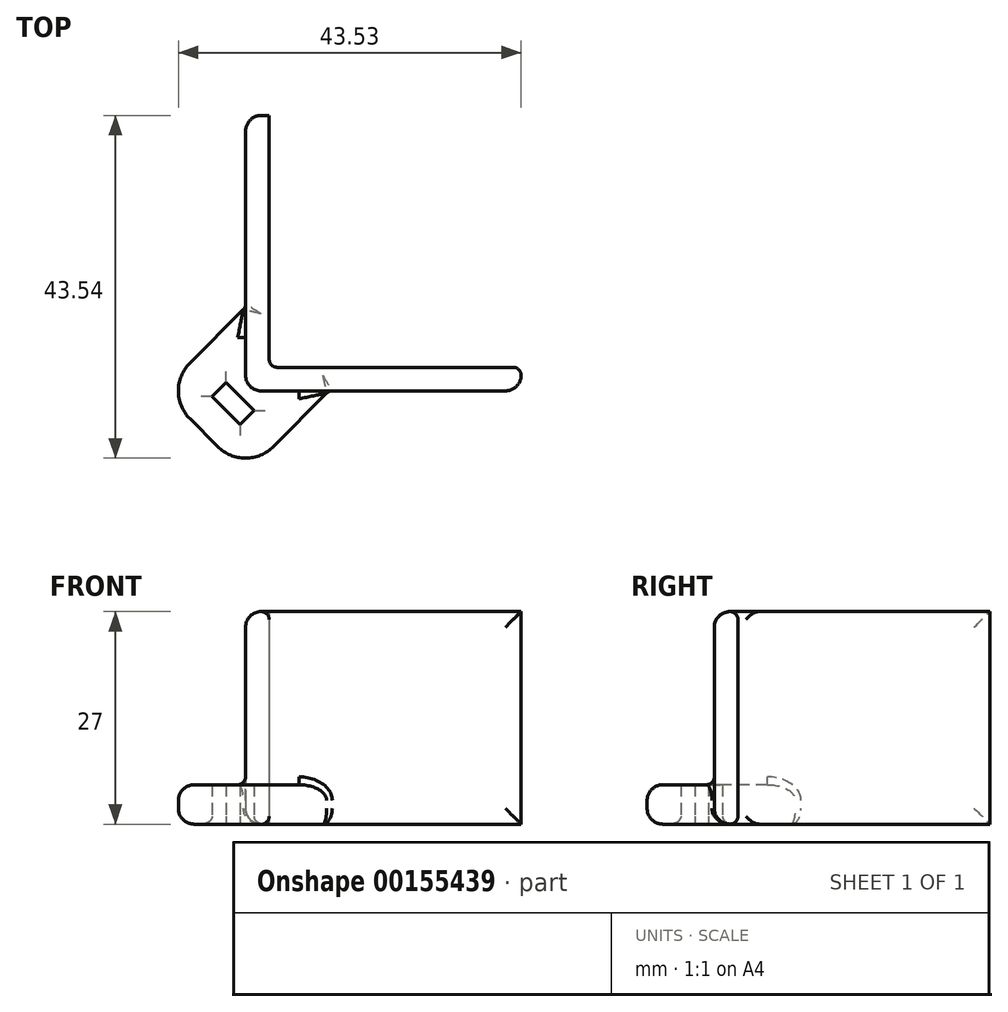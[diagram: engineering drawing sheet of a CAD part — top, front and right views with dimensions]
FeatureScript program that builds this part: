
annotation { "Feature Type Name" : "Feature", "Feature Type Description" : "" }
export const myFeature = defineFeature(function(context is Context, id is Id, definition is map)
    precondition{}
    {
        {
            var Q0;
            Q0=qCreatedBy(makeId("Top.planeOp"),FACE);
            var sketch = newSketch(context, id + "F0", { "sketchPlane" : qUnion([Q0])});
            skLineSegment(sketch, "E0", {"start": v(2.48, 21.6) * mm, "end": v(2.48, -13.4) * mm});
            skLineSegment(sketch, "E1", {"start": v(2.48, -13.4) * mm, "end": v(37.48, -13.4) * mm});
            skLineSegment(sketch, "E2", {"start": v(37.48, -13.4) * mm, "end": v(37.48, -10.4) * mm});
            skLineSegment(sketch, "E3", {"start": v(37.48, -10.4) * mm, "end": v(5.48, -10.4) * mm});
            skLineSegment(sketch, "E4", {"start": v(5.48, -10.4) * mm, "end": v(5.48, 21.6) * mm});
            skLineSegment(sketch, "E5", {"start": v(5.48, 21.6) * mm, "end": v(2.48, 21.6) * mm});
            skLineSegment(sketch, "E6", {"start": v(2.48, -2.8) * mm, "end": v(-8.13, -13.4) * mm});
            skLineSegment(sketch, "E7", {"start": v(-8.13, -13.4) * mm, "end": v(2.48, -24) * mm});
            skLineSegment(sketch, "E8", {"start": v(2.48, -24) * mm, "end": v(13.09, -13.4) * mm});
            skPoint(sketch, "E9.endSnap0", {"position": v(-2.82, -18.7) * mm});
            skLineSegment(sketch, "E10", {"start": v(0, -12.35) * mm, "end": v(3.54, -15.88) * mm});
            skLineSegment(sketch, "E11", {"start": v(3.54, -15.88) * mm, "end": v(1.77, -17.65) * mm});
            skLineSegment(sketch, "E12", {"start": v(1.77, -17.65) * mm, "end": v(-1.77, -14.11) * mm});
            skLineSegment(sketch, "E13", {"start": v(-1.77, -14.11) * mm, "end": v(0, -12.35) * mm});
            skSolve(sketch);
        }
        {
            var Q0;
            Q0=makeQuery(id+"F0.imprint","IMPRINT",FACE,{"disambiguationData":[TD([[makeQuery(id+"F0.imprint","IMPRINT",EDGE,{"derivedFrom":sQuery(id+"F0.wireOp",EDGE,"E0")}),1.0]])]});
            extrude(context, id + "F1", {"entities" : qUnion([Q0]), "depth" : 27 * mm});
        }
        {
            var Q0;
            Q0 = qSketchRegion(id + "F0", true);
            extrude(context, id + "F2", {"entities" : qUnion([Q0]), "operationType" : NewBodyOperationType.ADD, "depth" : 5 * mm});
        }
        {
            var Q0;
            Q0=makeQuery(id+"F1.opExtrude","SWEPT_EDGE",EDGE,{"disambiguationData":[OSD([sQuery(id+"F0.wireOp",EDGE,"E0"),sQuery(id+"F0.wireOp",EDGE,"E1")])]});
            var Q1;
            Q1=makeQuery(id+"F1.opExtrude","CAP_EDGE",EDGE,{"disambiguationData":[OSD([sQuery(id+"F0.wireOp",EDGE,"E1")])],"isStart":false});
            var Q2;
            Q2=makeQuery(id+"F1.opExtrude","CAP_EDGE",EDGE,{"disambiguationData":[OSD([sQuery(id+"F0.wireOp",EDGE,"E0")])],"isStart":false});
            var Q3;
            Q3=makeQuery(id+"F1.opExtrude","CAP_EDGE",EDGE,{"disambiguationData":[OSD([sQuery(id+"F0.wireOp",EDGE,"E1")])],"isStart":true});
            var Q4;
            Q4=makeQuery(id+"F1.opExtrude","SWEPT_EDGE",EDGE,{"disambiguationData":[OSD([sQuery(id+"F0.wireOp",EDGE,"E1"),sQuery(id+"F0.wireOp",EDGE,"E2")])]});
            var Q5;
            Q5=makeQuery(id+"F1.opExtrude","CAP_EDGE",EDGE,{"disambiguationData":[OSD([sQuery(id+"F0.wireOp",EDGE,"E0")])],"isStart":true});
            var Q6;
            Q6=makeQuery(id+"F1.opExtrude","SWEPT_EDGE",EDGE,{"disambiguationData":[OSD([sQuery(id+"F0.wireOp",EDGE,"E0"),sQuery(id+"F0.wireOp",EDGE,"E5")])]});
            var Q7;
            Q7=makeQuery(id+"F2.opExtrude","CAP_EDGE",EDGE,{"disambiguationData":[OSD([sQuery(id+"F0.wireOp",EDGE,"E6")])],"isStart":false});
            var Q8;
            Q8=makeQuery(id+"F2.opExtrude","CAP_EDGE",EDGE,{"disambiguationData":[OSD([sQuery(id+"F0.wireOp",EDGE,"E8")])],"isStart":false});
            var Q9;
            Q9=makeQuery(id+"F2.opExtrude","CAP_EDGE",EDGE,{"disambiguationData":[OSD([sQuery(id+"F0.wireOp",EDGE,"E7")])],"isStart":false});
            var Q10;
            Q10=makeQuery(id+"F2.opExtrude","CAP_EDGE",EDGE,{"disambiguationData":[OSD([sQuery(id+"F0.wireOp",EDGE,"E7")])],"isStart":true});
            var Q11;
            Q11=makeQuery(id+"F2.opExtrude","CAP_EDGE",EDGE,{"disambiguationData":[OSD([sQuery(id+"F0.wireOp",EDGE,"E6")])],"isStart":true});
            var Q12;
            Q12=makeQuery(id+"F2.opExtrude","CAP_EDGE",EDGE,{"disambiguationData":[OSD([sQuery(id+"F0.wireOp",EDGE,"E8")])],"isStart":true});
            fillet(context, id + "F3", {"entities" : qUnion([Q0, Q1, Q2, Q3, Q4, Q5, Q6, Q7, Q8, Q9, Q10, Q11, Q12]), "radius" : 2 * mm, "tangentPropagation" : true, "allowEdgeOverflow" : false});
        }
        {
            var Q0;
            Q0=makeQuery(id+"F2.opExtrude","SWEPT_EDGE",EDGE,{"disambiguationData":[OSD([sQuery(id+"F0.wireOp",EDGE,"E6"),sQuery(id+"F0.wireOp",EDGE,"E7")])]});
            var Q1;
            Q1=makeQuery(id+"F2.opExtrude","SWEPT_EDGE",EDGE,{"disambiguationData":[OSD([sQuery(id+"F0.wireOp",EDGE,"E7"),sQuery(id+"F0.wireOp",EDGE,"E8")])]});
            var Q2;
            Q2=makeQuery(id+"F2.opExtrude","SWEPT_EDGE",EDGE,{"disambiguationData":[OSD([sQuery(id+"F0.wireOp",EDGE,"E0"),sQuery(id+"F0.wireOp",EDGE,"E6")])]});
            fillet(context, id + "F4", {"entities" : qUnion([Q0, Q1, Q2]), "radius" : 5 * mm, "tangentPropagation" : true, "allowEdgeOverflow" : false});
        }
        {
            var Q0;
            {var subQ0=sQuery(id+"F0.wireOp",EDGE,"E5");var subQ1=sQuery(id+"F0.wireOp",EDGE,"E4");var subQ2=sQuery(id+"F0.wireOp",EDGE,"E3");var subQ3=sQuery(id+"F0.wireOp",EDGE,"E2");var subQ4=sQuery(id+"F0.wireOp",EDGE,"E1");var subQ5=sQuery(id+"F0.wireOp",EDGE,"E0");Q0=makeQuery(id+"F3.opFillet","BLEND_EDGE",EDGE,{"blendedFrom":[makeQuery(id+"F1.opExtrude","CAP_EDGE",EDGE,{"disambiguationData":[OSD([subQ5])],"isStart":true}),makeQuery(id+"F2.boolean.opBoolean","MERGE",FACE,{"derivedFrom":[makeQuery(id+"F1.opExtrude","CAP_FACE",FACE,{"disambiguationData":[OSD([subQ5,subQ4,subQ3,subQ2,subQ1,subQ0])],"isStart":true}),makeQuery(id+"F2.opExtrude","CAP_FACE",FACE,{"disambiguationData":[OSD([subQ5,subQ4,subQ3,subQ2,subQ1,subQ0,sQuery(id+"F0.wireOp",EDGE,"E6"),sQuery(id+"F0.wireOp",EDGE,"E7"),sQuery(id+"F0.wireOp",EDGE,"E8"),sQuery(id+"F0.wireOp",EDGE,"E10"),sQuery(id+"F0.wireOp",EDGE,"E11"),sQuery(id+"F0.wireOp",EDGE,"E12"),sQuery(id+"F0.wireOp",EDGE,"E13")])],"isStart":true})]})],"blendedInto":[makeQuery(id+"F2.boolean.opBoolean","MERGE",FACE,{"derivedFrom":[makeQuery(id+"F1.opExtrude","CAP_FACE",FACE,{"disambiguationData":[OSD([subQ5,subQ4,subQ3,subQ2,subQ1,subQ0])],"isStart":true}),makeQuery(id+"F2.opExtrude","CAP_FACE",FACE,{"disambiguationData":[OSD([subQ5,subQ4,subQ3,subQ2,subQ1,subQ0,sQuery(id+"F0.wireOp",EDGE,"E6"),sQuery(id+"F0.wireOp",EDGE,"E7"),sQuery(id+"F0.wireOp",EDGE,"E8"),sQuery(id+"F0.wireOp",EDGE,"E10"),sQuery(id+"F0.wireOp",EDGE,"E11"),sQuery(id+"F0.wireOp",EDGE,"E12"),sQuery(id+"F0.wireOp",EDGE,"E13")])],"isStart":true})]})]});}
            var Q1;
            Q1=makeQuery(id+"F1.opExtrude","SWEPT_FACE",FACE,{"disambiguationData":[OSD([sQuery(id+"F0.wireOp",EDGE,"E1")])]});
            var Q2;
            Q2=makeQuery(id+"F1.opExtrude","SWEPT_FACE",FACE,{"disambiguationData":[OSD([sQuery(id+"F0.wireOp",EDGE,"E3")])]});
            var Q3;
            {var subQ0=sQuery(id+"F0.wireOp",EDGE,"E10");var subQ1=sQuery(id+"F0.wireOp",EDGE,"E1");var subQ2=sQuery(id+"F0.wireOp",EDGE,"E0");Q3=makeQuery(id+"F4.opFillet","BLEND_EDGE",EDGE,{"blendedFrom":[makeQuery(id+"F3.opFillet","BLEND_EDGE",EDGE,{"blendedFrom":[makeQuery(id+"F1.opExtrude","SWEPT_EDGE",EDGE,{"disambiguationData":[OSD([subQ2,subQ1])]}),makeQuery(id+"F2.opExtrude","CAP_FACE",FACE,{"disambiguationData":[OSD([subQ2,subQ1,sQuery(id+"F0.wireOp",EDGE,"E2"),sQuery(id+"F0.wireOp",EDGE,"E3"),sQuery(id+"F0.wireOp",EDGE,"E4"),sQuery(id+"F0.wireOp",EDGE,"E5"),sQuery(id+"F0.wireOp",EDGE,"E6"),sQuery(id+"F0.wireOp",EDGE,"E7"),sQuery(id+"F0.wireOp",EDGE,"E8"),subQ0,sQuery(id+"F0.wireOp",EDGE,"E11"),sQuery(id+"F0.wireOp",EDGE,"E12"),sQuery(id+"F0.wireOp",EDGE,"E13")])],"isStart":false})],"blendedInto":[makeQuery(id+"F2.opExtrude","CAP_FACE",FACE,{"disambiguationData":[OSD([subQ2,subQ1,sQuery(id+"F0.wireOp",EDGE,"E2"),sQuery(id+"F0.wireOp",EDGE,"E3"),sQuery(id+"F0.wireOp",EDGE,"E4"),sQuery(id+"F0.wireOp",EDGE,"E5"),sQuery(id+"F0.wireOp",EDGE,"E6"),sQuery(id+"F0.wireOp",EDGE,"E7"),sQuery(id+"F0.wireOp",EDGE,"E8"),subQ0,sQuery(id+"F0.wireOp",EDGE,"E11"),sQuery(id+"F0.wireOp",EDGE,"E12"),sQuery(id+"F0.wireOp",EDGE,"E13")])],"isStart":false})]}),makeQuery(id+"F2.opExtrude","SWEPT_FACE",FACE,{"disambiguationData":[OSD([subQ0])]})],"blendedInto":[makeQuery(id+"F2.opExtrude","SWEPT_FACE",FACE,{"disambiguationData":[OSD([subQ0])]})]});}
            var Q4;
            {var subQ0=sQuery(id+"F0.wireOp",EDGE,"E13");var subQ1=sQuery(id+"F0.wireOp",EDGE,"E1");var subQ2=sQuery(id+"F0.wireOp",EDGE,"E0");Q4=makeQuery(id+"F4.opFillet","BLEND_EDGE",EDGE,{"blendedFrom":[makeQuery(id+"F3.opFillet","BLEND_EDGE",EDGE,{"blendedFrom":[makeQuery(id+"F1.opExtrude","SWEPT_EDGE",EDGE,{"disambiguationData":[OSD([subQ2,subQ1])]}),makeQuery(id+"F2.opExtrude","CAP_FACE",FACE,{"disambiguationData":[OSD([subQ2,subQ1,sQuery(id+"F0.wireOp",EDGE,"E2"),sQuery(id+"F0.wireOp",EDGE,"E3"),sQuery(id+"F0.wireOp",EDGE,"E4"),sQuery(id+"F0.wireOp",EDGE,"E5"),sQuery(id+"F0.wireOp",EDGE,"E6"),sQuery(id+"F0.wireOp",EDGE,"E7"),sQuery(id+"F0.wireOp",EDGE,"E8"),sQuery(id+"F0.wireOp",EDGE,"E10"),sQuery(id+"F0.wireOp",EDGE,"E11"),sQuery(id+"F0.wireOp",EDGE,"E12"),subQ0])],"isStart":false})],"blendedInto":[makeQuery(id+"F2.opExtrude","CAP_FACE",FACE,{"disambiguationData":[OSD([subQ2,subQ1,sQuery(id+"F0.wireOp",EDGE,"E2"),sQuery(id+"F0.wireOp",EDGE,"E3"),sQuery(id+"F0.wireOp",EDGE,"E4"),sQuery(id+"F0.wireOp",EDGE,"E5"),sQuery(id+"F0.wireOp",EDGE,"E6"),sQuery(id+"F0.wireOp",EDGE,"E7"),sQuery(id+"F0.wireOp",EDGE,"E8"),sQuery(id+"F0.wireOp",EDGE,"E10"),sQuery(id+"F0.wireOp",EDGE,"E11"),sQuery(id+"F0.wireOp",EDGE,"E12"),subQ0])],"isStart":false})]}),makeQuery(id+"F2.opExtrude","SWEPT_FACE",FACE,{"disambiguationData":[OSD([subQ0])]})],"blendedInto":[makeQuery(id+"F2.opExtrude","SWEPT_FACE",FACE,{"disambiguationData":[OSD([subQ0])]})]});}
            var Q5;
            {var subQ0=sQuery(id+"F0.wireOp",EDGE,"E12");var subQ1=sQuery(id+"F0.wireOp",EDGE,"E1");var subQ2=sQuery(id+"F0.wireOp",EDGE,"E0");Q5=makeQuery(id+"F4.opFillet","BLEND_EDGE",EDGE,{"blendedFrom":[makeQuery(id+"F3.opFillet","BLEND_EDGE",EDGE,{"blendedFrom":[makeQuery(id+"F1.opExtrude","SWEPT_EDGE",EDGE,{"disambiguationData":[OSD([subQ2,subQ1])]}),makeQuery(id+"F2.opExtrude","CAP_FACE",FACE,{"disambiguationData":[OSD([subQ2,subQ1,sQuery(id+"F0.wireOp",EDGE,"E2"),sQuery(id+"F0.wireOp",EDGE,"E3"),sQuery(id+"F0.wireOp",EDGE,"E4"),sQuery(id+"F0.wireOp",EDGE,"E5"),sQuery(id+"F0.wireOp",EDGE,"E6"),sQuery(id+"F0.wireOp",EDGE,"E7"),sQuery(id+"F0.wireOp",EDGE,"E8"),sQuery(id+"F0.wireOp",EDGE,"E10"),sQuery(id+"F0.wireOp",EDGE,"E11"),subQ0,sQuery(id+"F0.wireOp",EDGE,"E13")])],"isStart":false})],"blendedInto":[makeQuery(id+"F2.opExtrude","CAP_FACE",FACE,{"disambiguationData":[OSD([subQ2,subQ1,sQuery(id+"F0.wireOp",EDGE,"E2"),sQuery(id+"F0.wireOp",EDGE,"E3"),sQuery(id+"F0.wireOp",EDGE,"E4"),sQuery(id+"F0.wireOp",EDGE,"E5"),sQuery(id+"F0.wireOp",EDGE,"E6"),sQuery(id+"F0.wireOp",EDGE,"E7"),sQuery(id+"F0.wireOp",EDGE,"E8"),sQuery(id+"F0.wireOp",EDGE,"E10"),sQuery(id+"F0.wireOp",EDGE,"E11"),subQ0,sQuery(id+"F0.wireOp",EDGE,"E13")])],"isStart":false})]}),makeQuery(id+"F2.opExtrude","SWEPT_FACE",FACE,{"disambiguationData":[OSD([subQ0])]})],"blendedInto":[makeQuery(id+"F2.opExtrude","SWEPT_FACE",FACE,{"disambiguationData":[OSD([subQ0])]})]});}
            var Q6;
            {var subQ0=sQuery(id+"F0.wireOp",EDGE,"E11");var subQ1=sQuery(id+"F0.wireOp",EDGE,"E1");var subQ2=sQuery(id+"F0.wireOp",EDGE,"E0");Q6=makeQuery(id+"F4.opFillet","BLEND_EDGE",EDGE,{"blendedFrom":[makeQuery(id+"F3.opFillet","BLEND_EDGE",EDGE,{"blendedFrom":[makeQuery(id+"F1.opExtrude","SWEPT_EDGE",EDGE,{"disambiguationData":[OSD([subQ2,subQ1])]}),makeQuery(id+"F2.opExtrude","CAP_FACE",FACE,{"disambiguationData":[OSD([subQ2,subQ1,sQuery(id+"F0.wireOp",EDGE,"E2"),sQuery(id+"F0.wireOp",EDGE,"E3"),sQuery(id+"F0.wireOp",EDGE,"E4"),sQuery(id+"F0.wireOp",EDGE,"E5"),sQuery(id+"F0.wireOp",EDGE,"E6"),sQuery(id+"F0.wireOp",EDGE,"E7"),sQuery(id+"F0.wireOp",EDGE,"E8"),sQuery(id+"F0.wireOp",EDGE,"E10"),subQ0,sQuery(id+"F0.wireOp",EDGE,"E12"),sQuery(id+"F0.wireOp",EDGE,"E13")])],"isStart":false})],"blendedInto":[makeQuery(id+"F2.opExtrude","CAP_FACE",FACE,{"disambiguationData":[OSD([subQ2,subQ1,sQuery(id+"F0.wireOp",EDGE,"E2"),sQuery(id+"F0.wireOp",EDGE,"E3"),sQuery(id+"F0.wireOp",EDGE,"E4"),sQuery(id+"F0.wireOp",EDGE,"E5"),sQuery(id+"F0.wireOp",EDGE,"E6"),sQuery(id+"F0.wireOp",EDGE,"E7"),sQuery(id+"F0.wireOp",EDGE,"E8"),sQuery(id+"F0.wireOp",EDGE,"E10"),subQ0,sQuery(id+"F0.wireOp",EDGE,"E12"),sQuery(id+"F0.wireOp",EDGE,"E13")])],"isStart":false})]}),makeQuery(id+"F2.opExtrude","SWEPT_FACE",FACE,{"disambiguationData":[OSD([subQ0])]})],"blendedInto":[makeQuery(id+"F2.opExtrude","SWEPT_FACE",FACE,{"disambiguationData":[OSD([subQ0])]})]});}
            var Q7;
            Q7=makeQuery(id+"F2.opExtrude","CAP_EDGE",EDGE,{"disambiguationData":[OSD([sQuery(id+"F0.wireOp",EDGE,"E12")])],"isStart":true});
            var Q8;
            Q8=makeQuery(id+"F2.opExtrude","CAP_EDGE",EDGE,{"disambiguationData":[OSD([sQuery(id+"F0.wireOp",EDGE,"E11")])],"isStart":true});
            var Q9;
            Q9=makeQuery(id+"F2.opExtrude","CAP_EDGE",EDGE,{"disambiguationData":[OSD([sQuery(id+"F0.wireOp",EDGE,"E10")])],"isStart":true});
            var Q10;
            Q10=makeQuery(id+"F2.opExtrude","CAP_EDGE",EDGE,{"disambiguationData":[OSD([sQuery(id+"F0.wireOp",EDGE,"E13")])],"isStart":true});
            fillet(context, id + "F5", {"entities" : qUnion([Q0, Q1, Q2, Q3, Q4, Q5, Q6, Q7, Q8, Q9, Q10]), "radius" : 1 * mm, "tangentPropagation" : true, "allowEdgeOverflow" : false});
        }
    });
